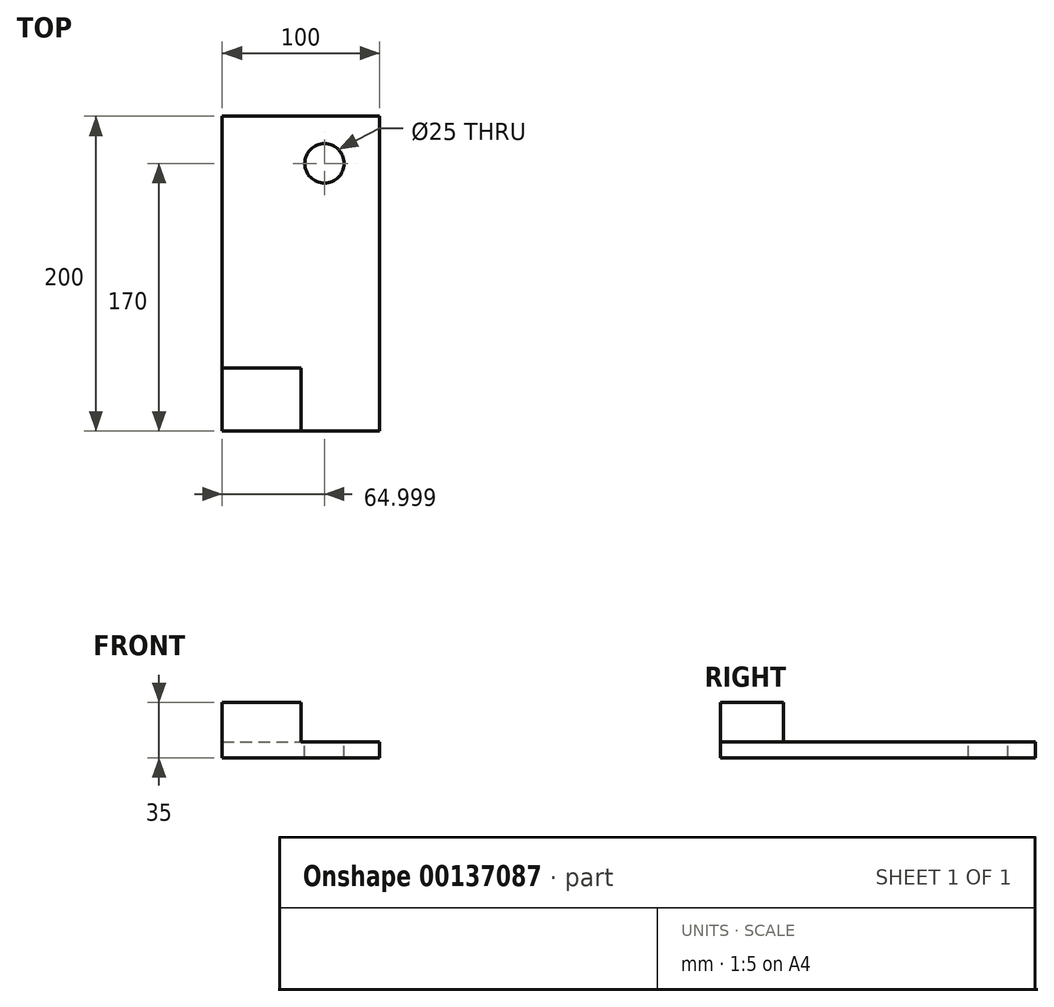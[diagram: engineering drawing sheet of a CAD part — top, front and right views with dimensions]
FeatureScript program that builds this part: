
annotation { "Feature Type Name" : "Feature", "Feature Type Description" : "" }
export const myFeature = defineFeature(function(context is Context, id is Id, definition is map)
    precondition{}
    {
        {
            var Q0;
            Q0=qCreatedBy(makeId("Top.planeOp"),FACE);
            var sketch = newSketch(context, id + "F0", { "sketchPlane" : qUnion([Q0])});
            skLineSegment(sketch, "E0.bottom", {"start": v(-63.23, 168.76) * mm, "end": v(36.77, 168.76) * mm});
            skLineSegment(sketch, "E0.top", {"start": v(-63.23, -31.24) * mm, "end": v(36.77, -31.24) * mm});
            skLineSegment(sketch, "E0.left", {"start": v(-63.23, 168.76) * mm, "end": v(-63.23, -31.24) * mm});
            skLineSegment(sketch, "E0.right", {"start": v(36.77, 168.76) * mm, "end": v(36.77, -31.24) * mm});
            skSolve(sketch);
        }
        {
            var Q0;
            Q0=makeQuery(id+"F0.imprint","IMPRINT",FACE,{"disambiguationData":[TD([[makeQuery(id+"F0.imprint","IMPRINT",EDGE,{"derivedFrom":sQuery(id+"F0.wireOp",EDGE,"E0.bottom")}),-1.0]])]});
            extrude(context, id + "F1", {"entities" : qUnion([Q0]), "depth" : 10 * mm});
        }
        {
            var Q0;
            Q0=makeQuery(id+"F1.opExtrude","CAP_FACE",FACE,{"disambiguationData":[OSD([sQuery(id+"F0.wireOp",EDGE,"E0.bottom"),sQuery(id+"F0.wireOp",EDGE,"E0.top"),sQuery(id+"F0.wireOp",EDGE,"E0.left"),sQuery(id+"F0.wireOp",EDGE,"E0.right")])],"isStart":false});
            var sketch = newSketch(context, id + "F2", { "sketchPlane" : qUnion([Q0])});
            skLineSegment(sketch, "E1.bottom", {"start": v(-63.23, -31.24) * mm, "end": v(-13.23, -31.24) * mm});
            skLineSegment(sketch, "E1.top", {"start": v(-63.23, 8.76) * mm, "end": v(-13.23, 8.76) * mm});
            skLineSegment(sketch, "E1.left", {"start": v(-63.23, -31.24) * mm, "end": v(-63.23, 8.76) * mm});
            skLineSegment(sketch, "E1.right", {"start": v(-13.23, -31.24) * mm, "end": v(-13.23, 8.76) * mm});
            skSolve(sketch);
        }
        {
            var Q0;
            Q0=makeQuery(id+"F2.imprint","IMPRINT",FACE,{"disambiguationData":[TD([[makeQuery(id+"F2.imprint","IMPRINT",EDGE,{"derivedFrom":sQuery(id+"F2.wireOp",EDGE,"E1.bottom")}),1.0]])]});
            extrude(context, id + "F3", {"entities" : qUnion([Q0]), "operationType" : NewBodyOperationType.ADD, "depth" : 25 * mm});
        }
        {
            var Q0;
            Q0=makeQuery(id+"F1.opExtrude","CAP_FACE",FACE,{"disambiguationData":[OSD([sQuery(id+"F0.wireOp",EDGE,"E0.bottom"),sQuery(id+"F0.wireOp",EDGE,"E0.top"),sQuery(id+"F0.wireOp",EDGE,"E0.left"),sQuery(id+"F0.wireOp",EDGE,"E0.right")])],"isStart":false});
            var sketch = newSketch(context, id + "F4", { "sketchPlane" : qUnion([Q0])});
            skCircle(sketch, "E2", {"center": v(1.77, 138.76) * mm, "radius": 12.5 * mm});
            skSolve(sketch);
        }
        {
            var Q0;
            Q0=makeQuery(id+"F4.imprint","IMPRINT",FACE,{"disambiguationData":[TD([[makeQuery(id+"F4.imprint","IMPRINT",EDGE,{"derivedFrom":sQuery(id+"F4.wireOp",EDGE,"E2")}),1.0]])]});
            extrude(context, id + "F5", {"entities" : qUnion([Q0]), "operationType" : NewBodyOperationType.REMOVE, "endBound" : BoundingType.THROUGH_ALL, "oppositeDirection" : true, "depth" : 25 * mm});
        }
    });
